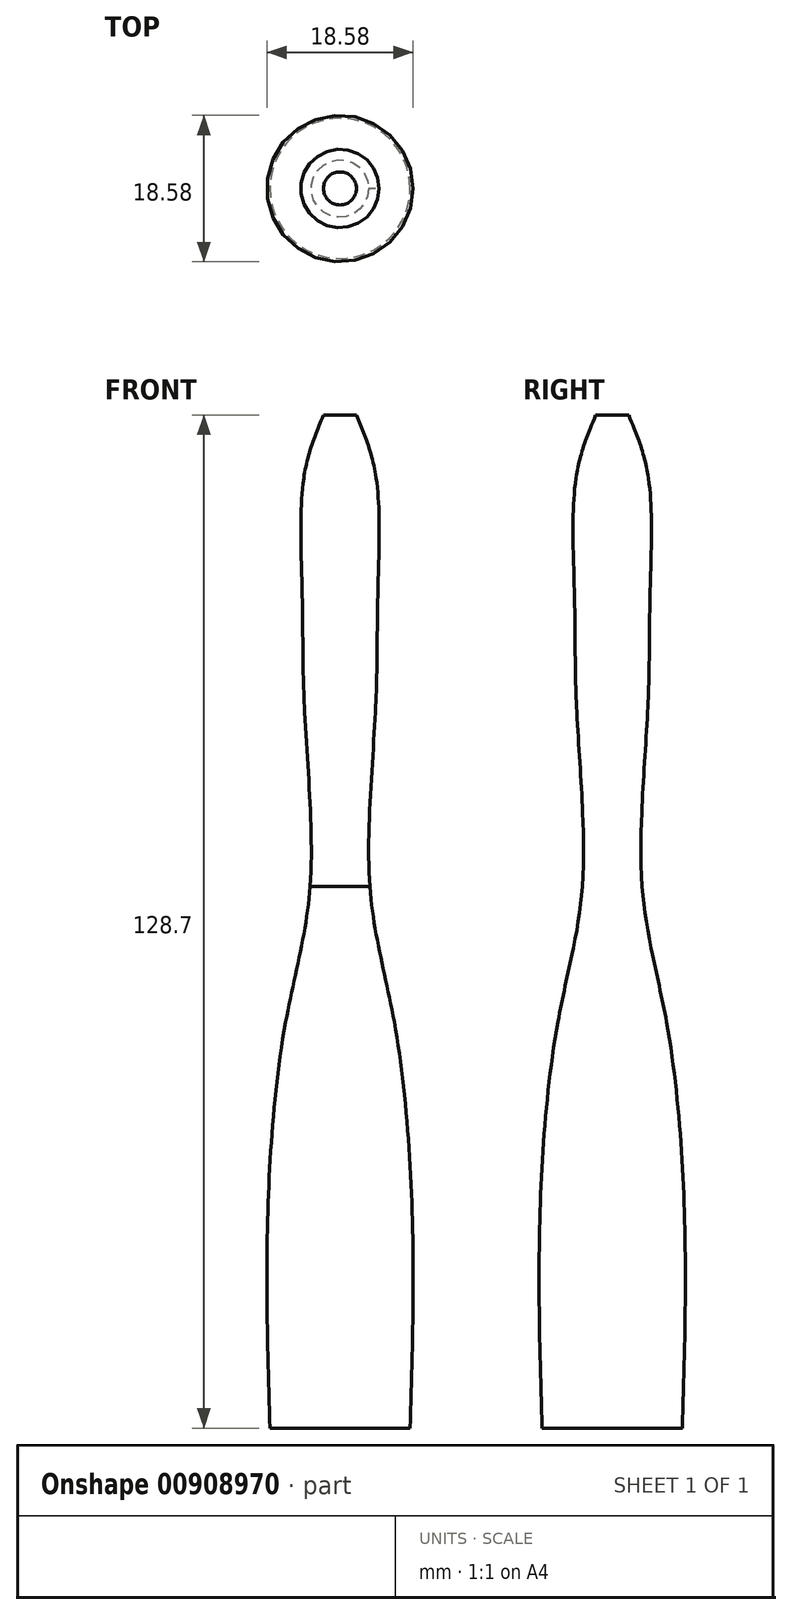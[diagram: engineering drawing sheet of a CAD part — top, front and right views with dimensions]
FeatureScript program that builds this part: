
annotation { "Feature Type Name" : "Feature", "Feature Type Description" : "" }
export const myFeature = defineFeature(function(context is Context, id is Id, definition is map)
    precondition{}
    {
        {
            var Q0;
            Q0=qCreatedBy(makeId("Front.planeOp"),FACE);
            var sketch = newSketch(context, id + "F0", { "sketchPlane" : qUnion([Q0])});
            skLineSegment(sketch, "E0", {"start": v(0, 67.9) * mm, "end": v(0, -60.8) * mm});
            skLineSegment(sketch, "E1", {"start": v(0, -60.8) * mm, "end": v(8.9, -60.8) * mm});
            skLineSegment(sketch, "E2", {"start": v(0, -34.4) * mm, "end": v(9.2, -34.4) * mm});
            skLineSegment(sketch, "E3", {"start": v(0, -9.2) * mm, "end": v(6.9, -9.2) * mm});
            skLineSegment(sketch, "E4", {"start": v(0, 8) * mm, "end": v(3.8, 8) * mm});
            skLineSegment(sketch, "E5", {"start": v(0, 30.2) * mm, "end": v(4.5, 30.2) * mm});
            skLineSegment(sketch, "E6", {"start": v(0, 44.3) * mm, "end": v(4.8, 44.3) * mm});
            skLineSegment(sketch, "E7", {"start": v(0, 59.9) * mm, "end": v(4.6, 59.9) * mm});
            skLineSegment(sketch, "E8", {"start": v(0, 67.9) * mm, "end": v(2.1, 67.9) * mm});
            skFitSpline(sketch, "E9", {"points": [v(2.1, 67.9) * mm, v(4.6, 59.9) * mm, v(4.8, 45.12) * mm, v(4.5, 30.2) * mm, v(3.8, 8) * mm, v(6.9, -9.2) * mm, v(9.2, -34.4) * mm, v(8.9, -60.8) * mm], "startDerivative": vector(31.12, -74.08) * mm, "endDerivative": vector(-4.68, -150.84) * mm});
            skSolve(sketch);
        }
        {
            var Q0;
            Q0 = qSketchRegion(id + "F0", true);
            var Q1;
            Q1=sQuery(id+"F0.wireOp",EDGE,"E0");
            revolve(context, id + "F1", {"surfaceOperationType" : NewSurfaceOperationType.NEW, "entities" : qUnion([Q0]), "axis" : qUnion([Q1]), "revolveType" : RevolveType.FULL});
        }
    });
